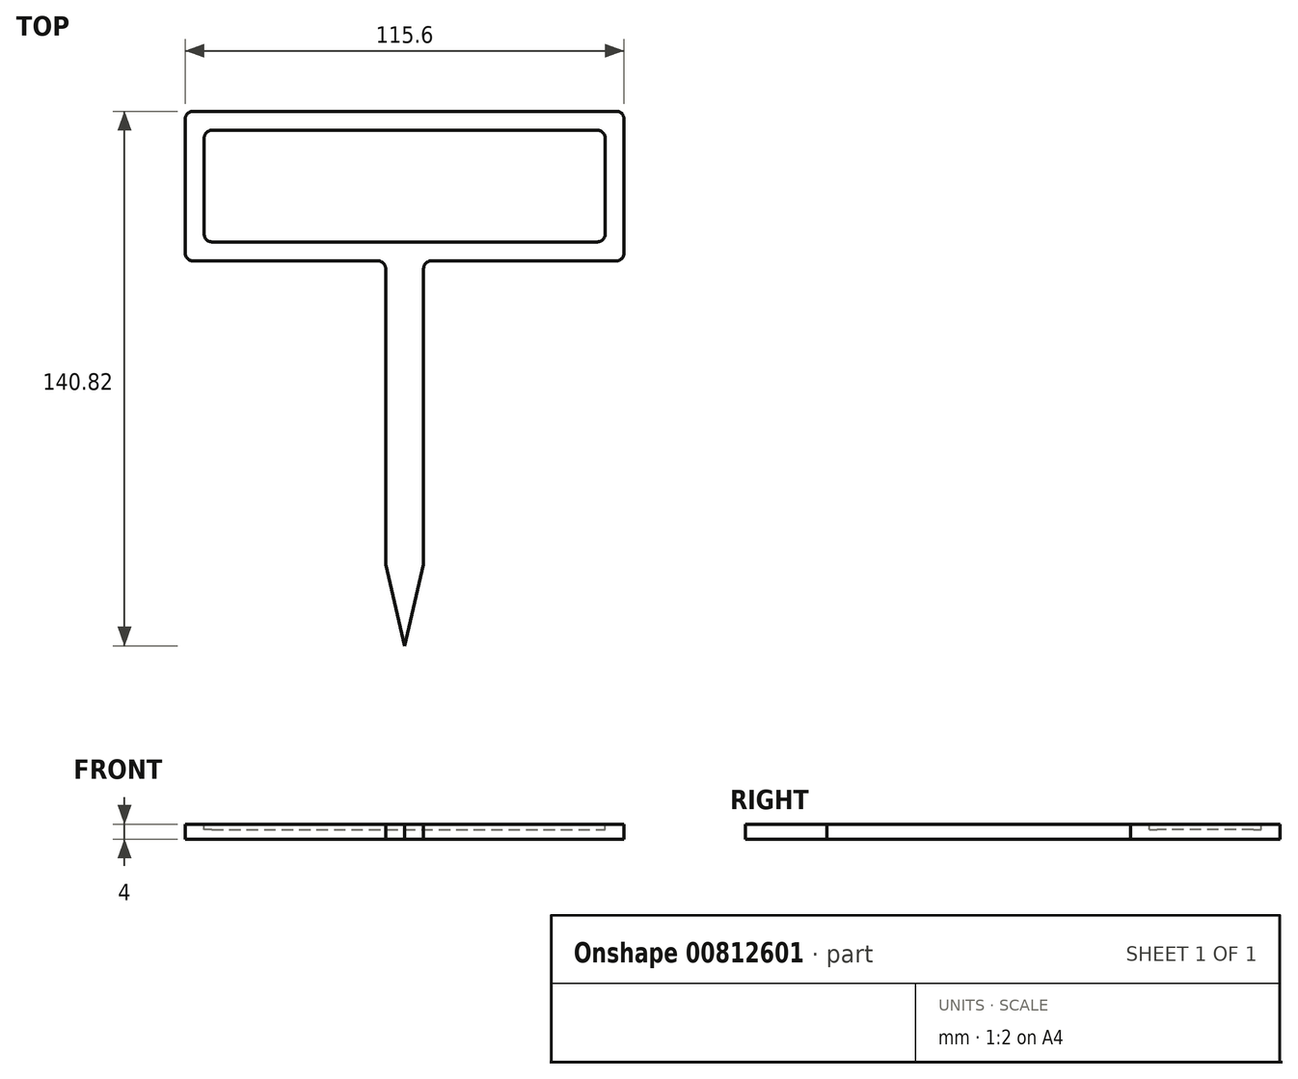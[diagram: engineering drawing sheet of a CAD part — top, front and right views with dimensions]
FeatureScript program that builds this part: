
annotation { "Feature Type Name" : "Feature", "Feature Type Description" : "" }
export const myFeature = defineFeature(function(context is Context, id is Id, definition is map)
    precondition{}
    {
        {
            var Q0;
            Q0=qCreatedBy(makeId("Top.planeOp"),FACE);
            var sketch = newSketch(context, id + "F0", { "sketchPlane" : qUnion([Q0])});
            skLineSegment(sketch, "E0.bottom", {"start": v(-52.8, 14.7) * mm, "end": v(52.8, 14.7) * mm});
            skLineSegment(sketch, "E0.top", {"start": v(-52.8, -14.7) * mm, "end": v(52.8, -14.7) * mm});
            skLineSegment(sketch, "E0.left", {"start": v(-52.8, 14.7) * mm, "end": v(-52.8, -14.7) * mm});
            skLineSegment(sketch, "E0.right", {"start": v(52.8, 14.7) * mm, "end": v(52.8, -14.7) * mm});
            skLineSegment(sketch, "E1.0", {"start": v(-57.8, 19.7) * mm, "end": v(57.8, 19.7) * mm});
            skLineSegment(sketch, "E1.1", {"start": v(-57.8, 19.7) * mm, "end": v(-57.8, -19.7) * mm});
            skLineSegment(sketch, "E1.2", {"start": v(-57.8, -19.7) * mm, "end": v(57.8, -19.7) * mm});
            skLineSegment(sketch, "E1.3", {"start": v(57.8, 19.7) * mm, "end": v(57.8, -19.7) * mm});
            skLineSegment(sketch, "E2.bottom", {"start": v(-5, -19.7) * mm, "end": v(5, -19.7) * mm});
            skLineSegment(sketch, "E2.top", {"start": v(-5, -99.7) * mm, "end": v(5, -99.7) * mm});
            skLineSegment(sketch, "E2.left", {"start": v(-5, -19.7) * mm, "end": v(-5, -99.7) * mm});
            skLineSegment(sketch, "E2.right", {"start": v(5, -19.7) * mm, "end": v(5, -99.7) * mm});
            skLineSegment(sketch, "E3", {"start": v(0, 0) * mm, "end": v(0, -199.09) * mm, "construction": true});
            skLineSegment(sketch, "E4", {"start": v(-5, -99.7) * mm, "end": v(0, -121.12) * mm});
            skLineSegment(sketch, "E5", {"start": v(0, -121.12) * mm, "end": v(5, -99.7) * mm});
            skSolve(sketch);
        }
        {
            var Q0;
            Q0=makeQuery(id+"F0.imprint","IMPRINT",FACE,{"disambiguationData":[TD([[makeQuery(id+"F0.imprint","IMPRINT",EDGE,{"derivedFrom":sQuery(id+"F0.wireOp",EDGE,"E0.bottom")}),1.0]])]});
            var Q1;
            Q1=makeQuery(id+"F0.imprint","IMPRINT",FACE,{"disambiguationData":[TD([[makeQuery(id+"F0.imprint","IMPRINT",EDGE,{"derivedFrom":sQuery(id+"F0.wireOp",EDGE,"E0.bottom")}),-1.0]])]});
            var Q2;
            Q2=makeQuery(id+"F0.imprint","IMPRINT",FACE,{"disambiguationData":[TD([[makeQuery(id+"F0.imprint","IMPRINT",EDGE,{"derivedFrom":sQuery(id+"F0.wireOp",EDGE,"E2.top")}),1.0]])]});
            var Q3;
            Q3=makeQuery(id+"F0.imprint","IMPRINT",FACE,{"disambiguationData":[TD([[makeQuery(id+"F0.imprint","IMPRINT",EDGE,{"derivedFrom":sQuery(id+"F0.wireOp",EDGE,"E2.top")}),-1.0]])]});
            extrude(context, id + "F1", {"entities" : qUnion([Q0, Q1, Q2, Q3]), "depth" : 4 * mm, "offsetDistance" : 25 * mm});
        }
        {
            var Q0;
            Q0=makeQuery(id+"F1.opExtrude","CAP_FACE",FACE,{"disambiguationData":[OSD([sQuery(id+"F0.wireOp",EDGE,"E1.0"),sQuery(id+"F0.wireOp",EDGE,"E1.1"),sQuery(id+"F0.wireOp",EDGE,"E1.2"),sQuery(id+"F0.wireOp",EDGE,"E1.3"),sQuery(id+"F0.wireOp",EDGE,"E2.left"),sQuery(id+"F0.wireOp",EDGE,"E2.right"),sQuery(id+"F0.wireOp",EDGE,"E4"),sQuery(id+"F0.wireOp",EDGE,"E5")])],"isStart":false});
            var sketch = newSketch(context, id + "F2", { "sketchPlane" : qUnion([Q0])});
            skLineSegment(sketch, "E6.0", {"start": v(-52.8, -14.7) * mm, "end": v(52.8, -14.7) * mm});
            skLineSegment(sketch, "E6.1", {"start": v(-52.8, 14.7) * mm, "end": v(-52.8, -14.7) * mm});
            skLineSegment(sketch, "E6.2", {"start": v(-52.8, 14.7) * mm, "end": v(52.8, 14.7) * mm});
            skLineSegment(sketch, "E6.3", {"start": v(52.8, 14.7) * mm, "end": v(52.8, -14.7) * mm});
            skSolve(sketch);
        }
        {
            var Q0;
            Q0=makeQuery(id+"F2.imprint","IMPRINT",FACE,{"disambiguationData":[TD([[makeQuery(id+"F2.imprint","IMPRINT",EDGE,{"derivedFrom":sQuery(id+"F2.wireOp",EDGE,"E6.0")}),1.0]])]});
            extrude(context, id + "F3", {"entities" : qUnion([Q0]), "operationType" : NewBodyOperationType.REMOVE, "oppositeDirection" : true, "depth" : 1.5 * mm, "offsetDistance" : 25 * mm});
        }
        {
            var Q0;
            Q0=makeQuery(id+"F1.opExtrude","SWEPT_EDGE",EDGE,{"disambiguationData":[OSD([sQuery(id+"F0.wireOp",EDGE,"E1.0"),sQuery(id+"F0.wireOp",EDGE,"E1.1")])]});
            var Q1;
            Q1=makeQuery(id+"F1.opExtrude","SWEPT_EDGE",EDGE,{"disambiguationData":[OSD([sQuery(id+"F0.wireOp",EDGE,"E1.1"),sQuery(id+"F0.wireOp",EDGE,"E1.2")])]});
            var Q2;
            Q2=makeQuery(id+"F1.opExtrude","SWEPT_EDGE",EDGE,{"disambiguationData":[OSD([sQuery(id+"F0.wireOp",EDGE,"E1.2"),sQuery(id+"F0.wireOp",EDGE,"E1.3")])]});
            var Q3;
            Q3=makeQuery(id+"F1.opExtrude","SWEPT_EDGE",EDGE,{"disambiguationData":[OSD([sQuery(id+"F0.wireOp",EDGE,"E1.0"),sQuery(id+"F0.wireOp",EDGE,"E1.3")])]});
            var Q4;
            Q4=makeQuery(id+"F3.boolean.opBoolean","COPY",EDGE,{"derivedFrom":makeQuery(id+"F3.opExtrude","SWEPT_EDGE",EDGE,{"disambiguationData":[OSD([sQuery(id+"F2.wireOp",EDGE,"E6.2"),sQuery(id+"F2.wireOp",EDGE,"E6.3")])]})});
            var Q5;
            Q5=makeQuery(id+"F3.boolean.opBoolean","COPY",EDGE,{"derivedFrom":makeQuery(id+"F3.opExtrude","SWEPT_EDGE",EDGE,{"disambiguationData":[OSD([sQuery(id+"F2.wireOp",EDGE,"E6.1"),sQuery(id+"F2.wireOp",EDGE,"E6.2")])]})});
            var Q6;
            Q6=makeQuery(id+"F3.boolean.opBoolean","COPY",EDGE,{"derivedFrom":makeQuery(id+"F3.opExtrude","SWEPT_EDGE",EDGE,{"disambiguationData":[OSD([sQuery(id+"F2.wireOp",EDGE,"E6.0"),sQuery(id+"F2.wireOp",EDGE,"E6.1")])]})});
            var Q7;
            Q7=makeQuery(id+"F3.boolean.opBoolean","COPY",EDGE,{"derivedFrom":makeQuery(id+"F3.opExtrude","SWEPT_EDGE",EDGE,{"disambiguationData":[OSD([sQuery(id+"F2.wireOp",EDGE,"E6.0"),sQuery(id+"F2.wireOp",EDGE,"E6.3")])]})});
            var Q8;
            Q8=makeQuery(id+"F1.opExtrude","SWEPT_EDGE",EDGE,{"disambiguationData":[OSD([sQuery(id+"F0.wireOp",EDGE,"E1.2"),sQuery(id+"F0.wireOp",EDGE,"E2.right")])]});
            var Q9;
            Q9=makeQuery(id+"F1.opExtrude","SWEPT_EDGE",EDGE,{"disambiguationData":[OSD([sQuery(id+"F0.wireOp",EDGE,"E1.2"),sQuery(id+"F0.wireOp",EDGE,"E2.left")])]});
            fillet(context, id + "F4", {"entities" : qUnion([Q0, Q1, Q2, Q3, Q4, Q5, Q6, Q7, Q8, Q9]), "radius" : 2 * mm, "tangentPropagation" : true, "allowEdgeOverflow" : false});
        }
    });
